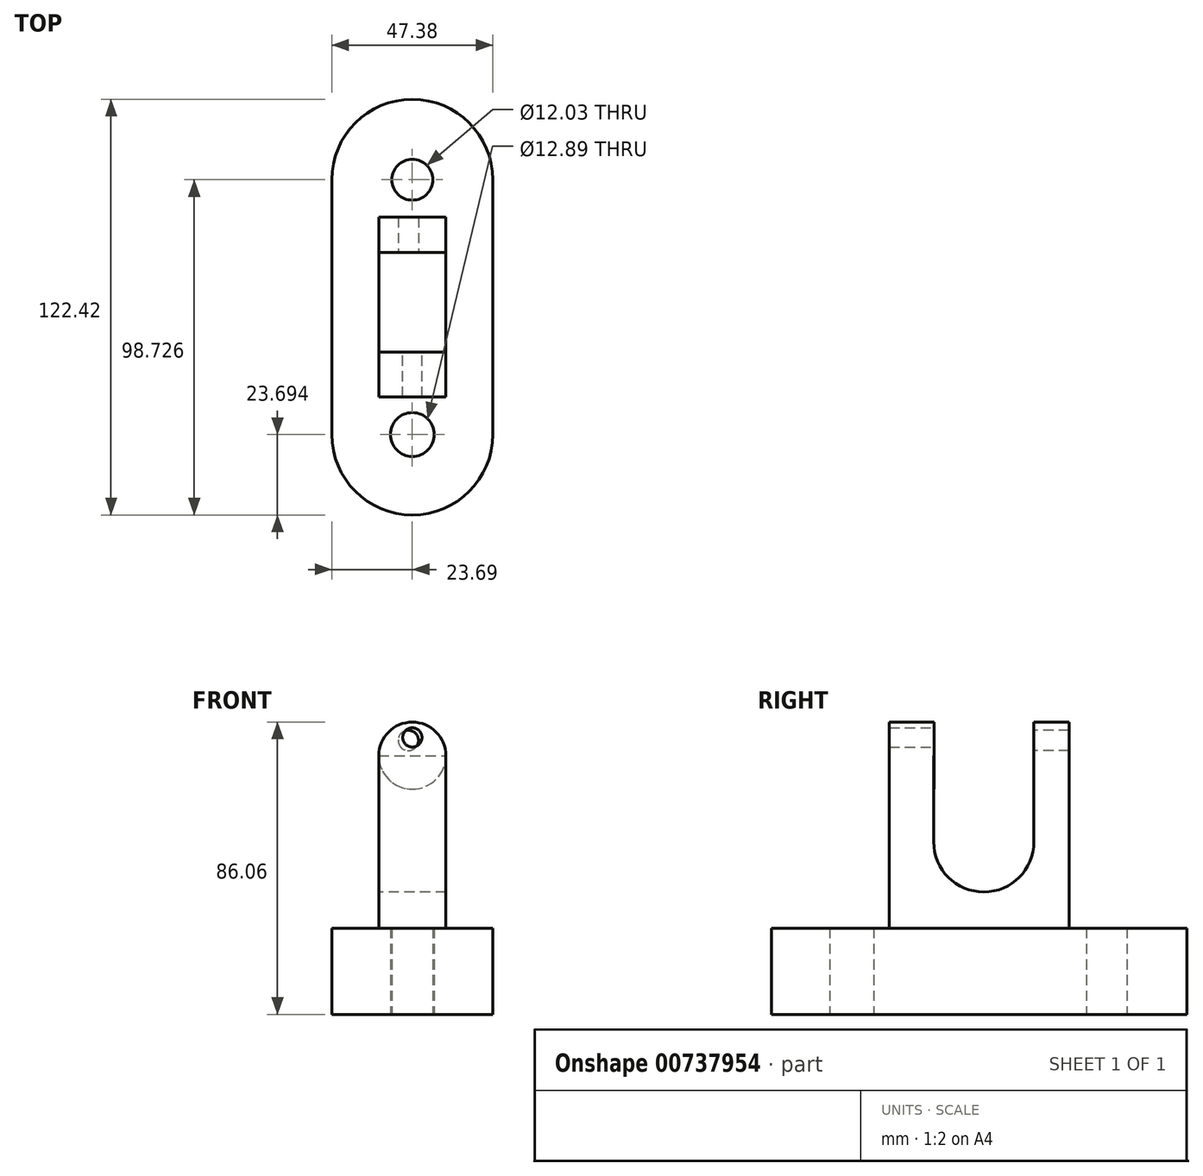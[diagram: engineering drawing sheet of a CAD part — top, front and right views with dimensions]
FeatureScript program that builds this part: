
annotation { "Feature Type Name" : "Feature", "Feature Type Description" : "" }
export const myFeature = defineFeature(function(context is Context, id is Id, definition is map)
    precondition{}
    {
        {
            var Q0;
            Q0=qCreatedBy(makeId("Top.planeOp"),FACE);
            var sketch = newSketch(context, id + "F0", { "sketchPlane" : qUnion([Q0])});
            skLineSegment(sketch, "E0.left", {"start": v(23.69, 37.52) * mm, "end": v(23.69, -37.52) * mm});
            skLineSegment(sketch, "E0.right", {"start": v(-23.69, 37.52) * mm, "end": v(-23.69, -37.52) * mm});
            skPoint(sketch, "E0.middle", {"position": v(0, 0) * mm});
            skArc(sketch, "E1", {"start": v(23.69, 37.52) * mm, "mid": v(0, 61.2) * mm, "end": v(-23.69, 37.52) * mm});
            skArc(sketch, "E2", {"start": v(-23.69, -37.52) * mm, "mid": v(0, -61.2) * mm, "end": v(23.69, -37.52) * mm});
            skCircle(sketch, "E3", {"center": v(0, 37.52) * mm, "radius": 6.02 * mm});
            skCircle(sketch, "E4", {"center": v(0, -37.52) * mm, "radius": 6.45 * mm});
            skSolve(sketch);
        }
        {
            var Q0;
            Q0=makeQuery(id+"F0.imprint","IMPRINT",FACE,{"disambiguationData":[TD([[makeQuery(id+"F0.imprint","IMPRINT",EDGE,{"derivedFrom":sQuery(id+"F0.wireOp",EDGE,"E0.left")}),-1.0]])]});
            extrude(context, id + "F1", {"entities" : qUnion([Q0]), "depth" : 25.4 * mm, "offsetDistance" : 25.4 * mm});
        }
        {
            var Q0;
            Q0=makeQuery(id+"F1.opExtrude","CAP_FACE",FACE,{"disambiguationData":[OSD([sQuery(id+"F0.wireOp",EDGE,"E0.left"),sQuery(id+"F0.wireOp",EDGE,"E0.right"),sQuery(id+"F0.wireOp",EDGE,"E1"),sQuery(id+"F0.wireOp",EDGE,"E2"),sQuery(id+"F0.wireOp",EDGE,"E3"),sQuery(id+"F0.wireOp",EDGE,"E4")])],"isStart":false});
            var sketch = newSketch(context, id + "F2", { "sketchPlane" : qUnion([Q0])});
            skLineSegment(sketch, "E5.bottom", {"start": v(9.86, 26.45) * mm, "end": v(-9.86, 26.45) * mm});
            skLineSegment(sketch, "E5.top", {"start": v(9.86, -26.45) * mm, "end": v(-9.86, -26.45) * mm});
            skLineSegment(sketch, "E5.left", {"start": v(9.86, 26.45) * mm, "end": v(9.86, -26.45) * mm});
            skLineSegment(sketch, "E5.right", {"start": v(-9.86, 26.45) * mm, "end": v(-9.86, -26.45) * mm});
            skPoint(sketch, "E5.middle", {"position": v(0, 0) * mm});
            skSolve(sketch);
        }
        {
            var Q0;
            Q0 = qSketchRegion(id + "F2", true);
            extrude(context, id + "F3", {"entities" : qUnion([Q0]), "operationType" : NewBodyOperationType.ADD, "depth" : 25.4 * mm, "offsetDistance" : 25.4 * mm});
        }
        {
            var Q0;
            Q0=makeQuery(id+"F3.opExtrude","CAP_FACE",FACE,{"disambiguationData":[OSD([sQuery(id+"F2.wireOp",EDGE,"E5.bottom"),sQuery(id+"F2.wireOp",EDGE,"E5.top"),sQuery(id+"F2.wireOp",EDGE,"E5.left"),sQuery(id+"F2.wireOp",EDGE,"E5.right")])],"isStart":false});
            var sketch = newSketch(context, id + "F4", { "sketchPlane" : qUnion([Q0])});
            skLineSegment(sketch, "E6", {"start": v(9.86, -13.41) * mm, "end": v(-9.86, -13.41) * mm});
            skLineSegment(sketch, "E7", {"start": v(-9.86, 16.1) * mm, "end": v(9.86, 16.1) * mm});
            skSolve(sketch);
        }
        {
            var Q0;
            {var subQ0=sQuery(id+"F4.wireOp",EDGE,"E6");Q0=makeQuery(id+"F4.imprint","IMPRINT",FACE,{"disambiguationData":[TD([[makeQuery(id+"F4.imprint","IMPRINT",EDGE,{"derivedFrom":subQ0}),1.0]])]});}
            var sketch = newSketch(context, id + "F5", { "sketchPlane" : qUnion([Q0])});
            skSolve(sketch);
        }
        {
            var Q0;
            {var subQ0=sQuery(id+"F4.wireOp",EDGE,"E6");Q0=makeQuery(id+"F5.imprint","IMPRINT",FACE,{"disambiguationData":[TD([[makeQuery(id+"F5.imprint","IMPRINT",EDGE,{"derivedFrom":makeQuery(id+"F4.imprint","IMPRINT",EDGE,{"derivedFrom":subQ0})}),1.0]])]});}
            extrude(context, id + "F6", {"entities" : qUnion([Q0]), "operationType" : NewBodyOperationType.ADD, "depth" : 25.4 * mm, "offsetDistance" : 25.4 * mm});
        }
        {
            var Q0;
            {var subQ0=sQuery(id+"F4.wireOp",EDGE,"E7");Q0=makeQuery(id+"F4.imprint","IMPRINT",FACE,{"disambiguationData":[TD([[makeQuery(id+"F4.imprint","IMPRINT",EDGE,{"derivedFrom":subQ0}),1.0]])]});}
            extrude(context, id + "F7", {"entities" : qUnion([Q0]), "operationType" : NewBodyOperationType.ADD, "depth" : 25.4 * mm, "offsetDistance" : 25.4 * mm});
        }
        {
            var Q0;
            {var subQ0=sQuery(id+"F2.wireOp",EDGE,"E5.top");Q0=makeQuery(id+"F6.boolean.opBoolean","MERGE",FACE,{"derivedFrom":[makeQuery(id+"F3.opExtrude","SWEPT_FACE",FACE,{"disambiguationData":[OSD([subQ0])]}),makeQuery(id+"F6.opExtrude","SWEPT_FACE",FACE,{"disambiguationData":[OSD([subQ0])]})]});}
            var sketch = newSketch(context, id + "F8", { "sketchPlane" : qUnion([Q0])});
            skCircle(sketch, "E8", {"center": v(0, 76.2) * mm, "radius": 9.86 * mm});
            skSolve(sketch);
        }
        {
            var Q0;
            Q0 = qSketchRegion(id + "F8", true);
            extrude(context, id + "F9", {"entities" : qUnion([Q0]), "operationType" : NewBodyOperationType.ADD, "oppositeDirection" : true, "depth" : 13.2 * mm, "offsetDistance" : 25.4 * mm});
        }
        {
            var Q0;
            Q0=makeQuery(id+"F9.opExtrude","CAP_FACE",FACE,{"disambiguationData":[OSD([sQuery(id+"F8.wireOp",EDGE,"E8")])],"isStart":false});
            var sketch = newSketch(context, id + "F10", { "sketchPlane" : qUnion([Q0])});
            skSolve(sketch);
        }
        {
            var Q0;
            {var subQ0=sQuery(id+"F2.wireOp",EDGE,"E5.bottom");Q0=makeQuery(id+"F7.boolean.opBoolean","MERGE",FACE,{"derivedFrom":[makeQuery(id+"F3.opExtrude","SWEPT_FACE",FACE,{"disambiguationData":[OSD([subQ0])]}),makeQuery(id+"F7.opExtrude","SWEPT_FACE",FACE,{"disambiguationData":[OSD([subQ0])]})]});}
            var sketch = newSketch(context, id + "F11", { "sketchPlane" : qUnion([Q0])});
            skCircle(sketch, "E9", {"center": v(0, 76.2) * mm, "radius": 9.86 * mm});
            skSolve(sketch);
        }
        {
            var Q0;
            {var subQ2=sQuery(id+"F2.wireOp",EDGE,"E5.bottom");var subQ3=makeQuery(id+"F7.opExtrude","CAP_EDGE",EDGE,{"disambiguationData":[OSD([subQ2])],"isStart":false});Q0=makeQuery(id+"F11.imprint","IMPRINT",FACE,{"disambiguationData":[TD([[makeQuery(id+"F11.imprint","IMPRINT",EDGE,{"derivedFrom":subQ3}),1.0]])]});}
            extrude(context, id + "F12", {"entities" : qUnion([Q0]), "operationType" : NewBodyOperationType.ADD, "oppositeDirection" : true, "depth" : 10.4 * mm, "offsetDistance" : 25.4 * mm});
        }
        {
            var Q0;
            Q0=makeQuery(id+"F12.opExtrude","CAP_FACE",FACE,{"disambiguationData":[OSD([sQuery(id+"F2.wireOp",EDGE,"E5.bottom"),sQuery(id+"F11.wireOp",EDGE,"E9")])],"isStart":false});
            var sketch = newSketch(context, id + "F13", { "sketchPlane" : qUnion([Q0])});
            skCircle(sketch, "E10", {"center": v(-1.17, 80.66) * mm, "radius": 2.99 * mm});
            skSolve(sketch);
        }
        {
            var Q0;
            Q0=makeQuery(id+"F13.imprint","IMPRINT",FACE,{"disambiguationData":[TD([[makeQuery(id+"F13.imprint","IMPRINT",EDGE,{"derivedFrom":sQuery(id+"F13.wireOp",EDGE,"E10")}),1.0]])]});
            extrude(context, id + "F14", {"entities" : qUnion([Q0]), "operationType" : NewBodyOperationType.REMOVE, "oppositeDirection" : true, "depth" : 25.4 * mm, "offsetDistance" : 25.4 * mm});
        }
        {
            var Q0;
            Q0=makeQuery(id+"F10.imprint","IMPRINT",FACE,{"disambiguationData":[TD([[makeQuery(id+"F10.imprint","IMPRINT",EDGE,{"derivedFrom":makeQuery(id+"F9.opExtrude","CAP_EDGE",EDGE,{"disambiguationData":[OSD([sQuery(id+"F8.wireOp",EDGE,"E8")])],"isStart":false})}),-1.0]])]});
            var sketch = newSketch(context, id + "F15", { "sketchPlane" : qUnion([Q0])});
            skCircle(sketch, "E11", {"center": v(0, 81.55) * mm, "radius": 2.84 * mm});
            skSolve(sketch);
        }
        {
            var Q0;
            Q0=makeQuery(id+"F15.imprint","IMPRINT",FACE,{"disambiguationData":[TD([[makeQuery(id+"F15.imprint","IMPRINT",EDGE,{"derivedFrom":sQuery(id+"F15.wireOp",EDGE,"E11")}),1.0]])]});
            extrude(context, id + "F16", {"entities" : qUnion([Q0]), "operationType" : NewBodyOperationType.REMOVE, "oppositeDirection" : true, "depth" : 25.4 * mm, "offsetDistance" : 25.4 * mm});
        }
        {
            var Q0;
            {var subQ0=sQuery(id+"F2.wireOp",EDGE,"E5.right");Q0=makeQuery(id+"F7.boolean.opBoolean","MERGE",FACE,{"derivedFrom":[makeQuery(id+"F6.boolean.opBoolean","MERGE",FACE,{"derivedFrom":[makeQuery(id+"F3.opExtrude","SWEPT_FACE",FACE,{"disambiguationData":[OSD([subQ0])]}),makeQuery(id+"F6.opExtrude","SWEPT_FACE",FACE,{"disambiguationData":[OSD([subQ0])]})]}),makeQuery(id+"F7.opExtrude","SWEPT_FACE",FACE,{"disambiguationData":[OSD([subQ0])]})]});}
            var sketch = newSketch(context, id + "F17", { "sketchPlane" : qUnion([Q0])});
            skCircle(sketch, "E12", {"center": v(-1.34, 50.8) * mm, "radius": 14.76 * mm});
            skSolve(sketch);
        }
        {
            var Q0;
            {var subQ1=sQuery(id+"F2.wireOp",EDGE,"E5.right");var subQ2=makeQuery(id+"F3.opExtrude","CAP_EDGE",EDGE,{"disambiguationData":[OSD([subQ1])],"isStart":false});Q0=makeQuery(id+"F17.imprint","IMPRINT",FACE,{"disambiguationData":[TD([[makeQuery(id+"F17.imprint","IMPRINT",EDGE,{"derivedFrom":subQ2}),-1.0]])]});}
            extrude(context, id + "F18", {"entities" : qUnion([Q0]), "operationType" : NewBodyOperationType.REMOVE, "oppositeDirection" : true, "depth" : 50.8 * mm, "offsetDistance" : 25.4 * mm});
        }
    });
